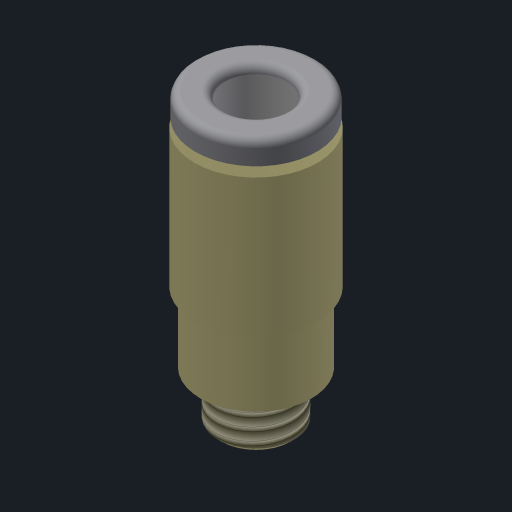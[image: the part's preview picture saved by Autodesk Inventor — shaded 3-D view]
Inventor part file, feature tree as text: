
AUTODESK INVENTOR PART (.ipt)
format: ipt  version: 2023 (Build 270158030, 158C)  size: 190,464 bytes
history: native  units: in
note: dims shown in document units (in); Inventor stores cm internally (conversion verified against a paired STEP export)
features: other x1, imported_body x1, thread x1
ambient origin geometry x8: Origin, YZ Plane, XZ Plane, XY Plane, X Axis, Y Axis, Z Axis, Center Point
bodies: Body1 (feature_tree)
feature tree (3):
  other  "Port"
  imported_body  "Base1"
  thread  "Thread1"  [1 undecoded]
note: 1 required parameter value undecoded (feature->parameter linkage not recoverable at this tier; creation-order binding heuristic only, values carry confidence <= 0.55)
